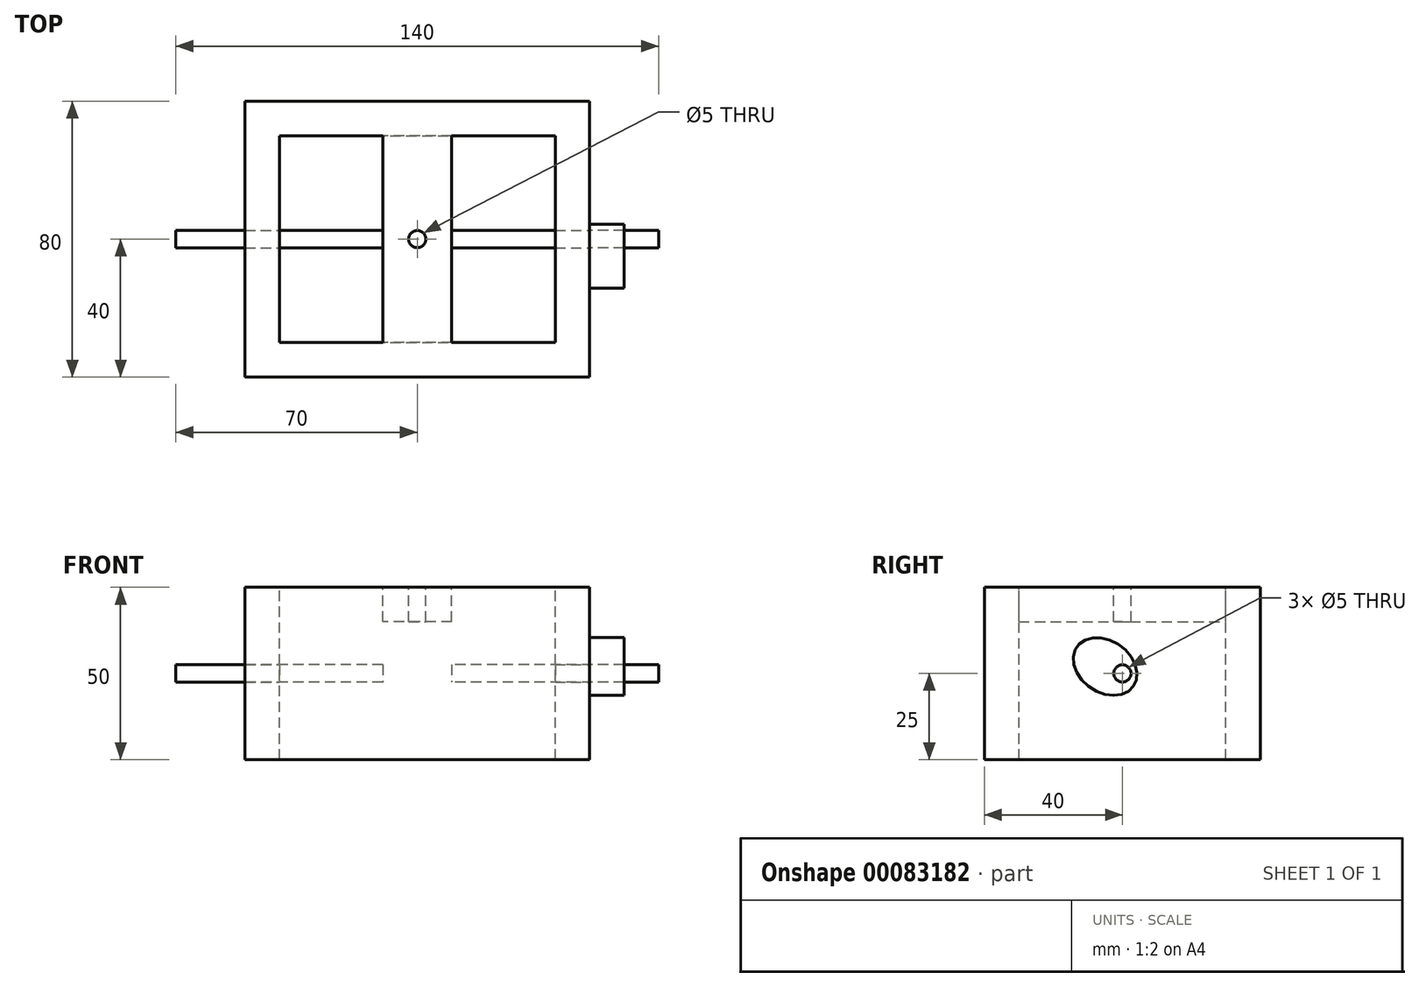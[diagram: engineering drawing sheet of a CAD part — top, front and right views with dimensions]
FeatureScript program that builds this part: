
annotation { "Feature Type Name" : "Feature", "Feature Type Description" : "" }
export const myFeature = defineFeature(function(context is Context, id is Id, definition is map)
    precondition{}
    {
        {
            var Q0;
            Q0=qCreatedBy(makeId("Front.planeOp"),FACE);
            var sketch = newSketch(context, id + "F0", { "sketchPlane" : qUnion([Q0])});
            skLineSegment(sketch, "E0.bottom", {"start": v(-50, -25) * mm, "end": v(50, -25) * mm});
            skLineSegment(sketch, "E0.top", {"start": v(-50, 25) * mm, "end": v(50, 25) * mm});
            skLineSegment(sketch, "E0.left", {"start": v(-50, -25) * mm, "end": v(-50, 25) * mm});
            skLineSegment(sketch, "E0.right", {"start": v(50, -25) * mm, "end": v(50, 25) * mm});
            skPoint(sketch, "E0.middle", {"position": v(0, 0) * mm});
            skSolve(sketch);
        }
        {
            var Q0;
            Q0 = qSketchRegion(id + "F0", true);
            extrude(context, id + "F1", {"entities" : qUnion([Q0]), "depth" : 80 * mm});
        }
        {
            var Q0;
            Q0=makeQuery(id+"F1.opExtrude","SWEPT_FACE",FACE,{"disambiguationData":[OSD([sQuery(id+"F0.wireOp",EDGE,"E0.top")])]});
            var sketch = newSketch(context, id + "F2", { "sketchPlane" : qUnion([Q0])});
            skLineSegment(sketch, "E1.bottom", {"start": v(-40, -10) * mm, "end": v(-10, -10) * mm});
            skLineSegment(sketch, "E1.top", {"start": v(-40, -70) * mm, "end": v(-10, -70) * mm});
            skLineSegment(sketch, "E1.left", {"start": v(-40, -10) * mm, "end": v(-40, -70) * mm});
            skLineSegment(sketch, "E1.right", {"start": v(40, -10) * mm, "end": v(40, -70) * mm});
            skLineSegment(sketch, "E2", {"start": v(10, -70) * mm, "end": v(10, -10) * mm});
            skLineSegment(sketch, "E3", {"start": v(-10, -70) * mm, "end": v(-10, -70) * mm});
            skLineSegment(sketch, "E4", {"start": v(10, -70) * mm, "end": v(40, -70) * mm});
            skLineSegment(sketch, "E5", {"start": v(-10, -70) * mm, "end": v(-10, -10) * mm});
            skLineSegment(sketch, "E6", {"start": v(10, -10) * mm, "end": v(40, -10) * mm});
            skSolve(sketch);
        }
        {
            var Q0;
            Q0 = qSketchRegion(id + "F2", true);
            extrude(context, id + "F3", {"entities" : qUnion([Q0]), "operationType" : NewBodyOperationType.REMOVE, "endBound" : BoundingType.THROUGH_ALL, "oppositeDirection" : true, "depth" : 25 * mm});
        }
        {
            var Q0;
            Q0=makeQuery(id+"F1.opExtrude","SWEPT_FACE",FACE,{"disambiguationData":[OSD([sQuery(id+"F0.wireOp",EDGE,"E0.right")])]});
            var sketch = newSketch(context, id + "F4", { "sketchPlane" : qUnion([Q0])});
            skCircle(sketch, "E7", {"center": v(-40, 0) * mm, "radius": 2.5 * mm});
            skSolve(sketch);
        }
        {
            var Q0;
            Q0 = qSketchRegion(id + "F4", true);
            extrude(context, id + "F5", {"entities" : qUnion([Q0]), "operationType" : NewBodyOperationType.REMOVE, "endBound" : BoundingType.THROUGH_ALL, "oppositeDirection" : true, "depth" : 25 * mm});
        }
        {
            var Q0;
            Q0 = qSketchRegion(id + "F4", true);
            extrude(context, id + "F6", {"entities" : qUnion([Q0]), "depth" : 20 * mm, "hasSecondDirection" : true, "secondDirectionOppositeDirection" : true, "secondDirectionDepth" : 120 * mm});
        }
        {
            var Q0;
            Q0=makeQuery(id+"F1.opExtrude","SWEPT_FACE",FACE,{"disambiguationData":[OSD([sQuery(id+"F0.wireOp",EDGE,"E0.right")])]});
            var sketch = newSketch(context, id + "F7", { "sketchPlane" : qUnion([Q0])});
            skEllipse(sketch, "E8", {"center": v(-45, 2) * mm, "majorRadius": 10 * mm, "minorRadius": 7.5 * mm, "majorAxis": v(0.82, -0.57)});
            skLineSegment(sketch, "E9", {"start": v(-45, 2) * mm, "end": v(-53.2, 7.74) * mm, "construction": true});
            skCircle(sketch, "E10", {"center": v(-40, 0) * mm, "radius": 2.5 * mm});
            skSolve(sketch);
        }
        {
            var Q0;
            Q0 = qSketchRegion(id + "F7", true);
            extrude(context, id + "F8", {"entities" : qUnion([Q0]), "depth" : 10 * mm});
        }
        {
            var Q0;
            Q0=makeQuery(id+"F1.opExtrude","SWEPT_FACE",FACE,{"disambiguationData":[OSD([sQuery(id+"F0.wireOp",EDGE,"E0.bottom")])]});
            var sketch = newSketch(context, id + "F9", { "sketchPlane" : qUnion([Q0])});
            skLineSegment(sketch, "E11.bottom", {"start": v(10, 10) * mm, "end": v(-10, 10) * mm});
            skLineSegment(sketch, "E11.top", {"start": v(10, 70) * mm, "end": v(-10, 70) * mm});
            skLineSegment(sketch, "E11.left", {"start": v(10, 10) * mm, "end": v(10, 70) * mm});
            skLineSegment(sketch, "E11.right", {"start": v(-10, 10) * mm, "end": v(-10, 70) * mm});
            skSolve(sketch);
        }
        {
            var Q0;
            Q0=makeQuery(id+"F9.imprint","IMPRINT",FACE,{"disambiguationData":[TD([[makeQuery(id+"F9.imprint","IMPRINT",EDGE,{"derivedFrom":sQuery(id+"F9.wireOp",EDGE,"E11.bottom")}),-1.0]])]});
            extrude(context, id + "F10", {"entities" : qUnion([Q0]), "operationType" : NewBodyOperationType.REMOVE, "oppositeDirection" : true, "depth" : 40 * mm});
        }
        {
            var Q0;
            Q0=makeQuery(id+"F1.opExtrude","SWEPT_FACE",FACE,{"disambiguationData":[OSD([sQuery(id+"F0.wireOp",EDGE,"E0.top")])]});
            var sketch = newSketch(context, id + "F11", { "sketchPlane" : qUnion([Q0])});
            skLineSegment(sketch, "E12", {"start": v(10, -70) * mm, "end": v(-10, -10) * mm, "construction": true});
            skLineSegment(sketch, "E13", {"start": v(-10, -70) * mm, "end": v(10, -10) * mm, "construction": true});
            skCircle(sketch, "E14", {"center": v(0, -40) * mm, "radius": 2.5 * mm});
            skSolve(sketch);
        }
        {
            var Q0;
            Q0 = qSketchRegion(id + "F11", true);
            extrude(context, id + "F12", {"entities" : qUnion([Q0]), "operationType" : NewBodyOperationType.REMOVE, "endBound" : BoundingType.THROUGH_ALL, "oppositeDirection" : true, "depth" : 25 * mm});
        }
    });
